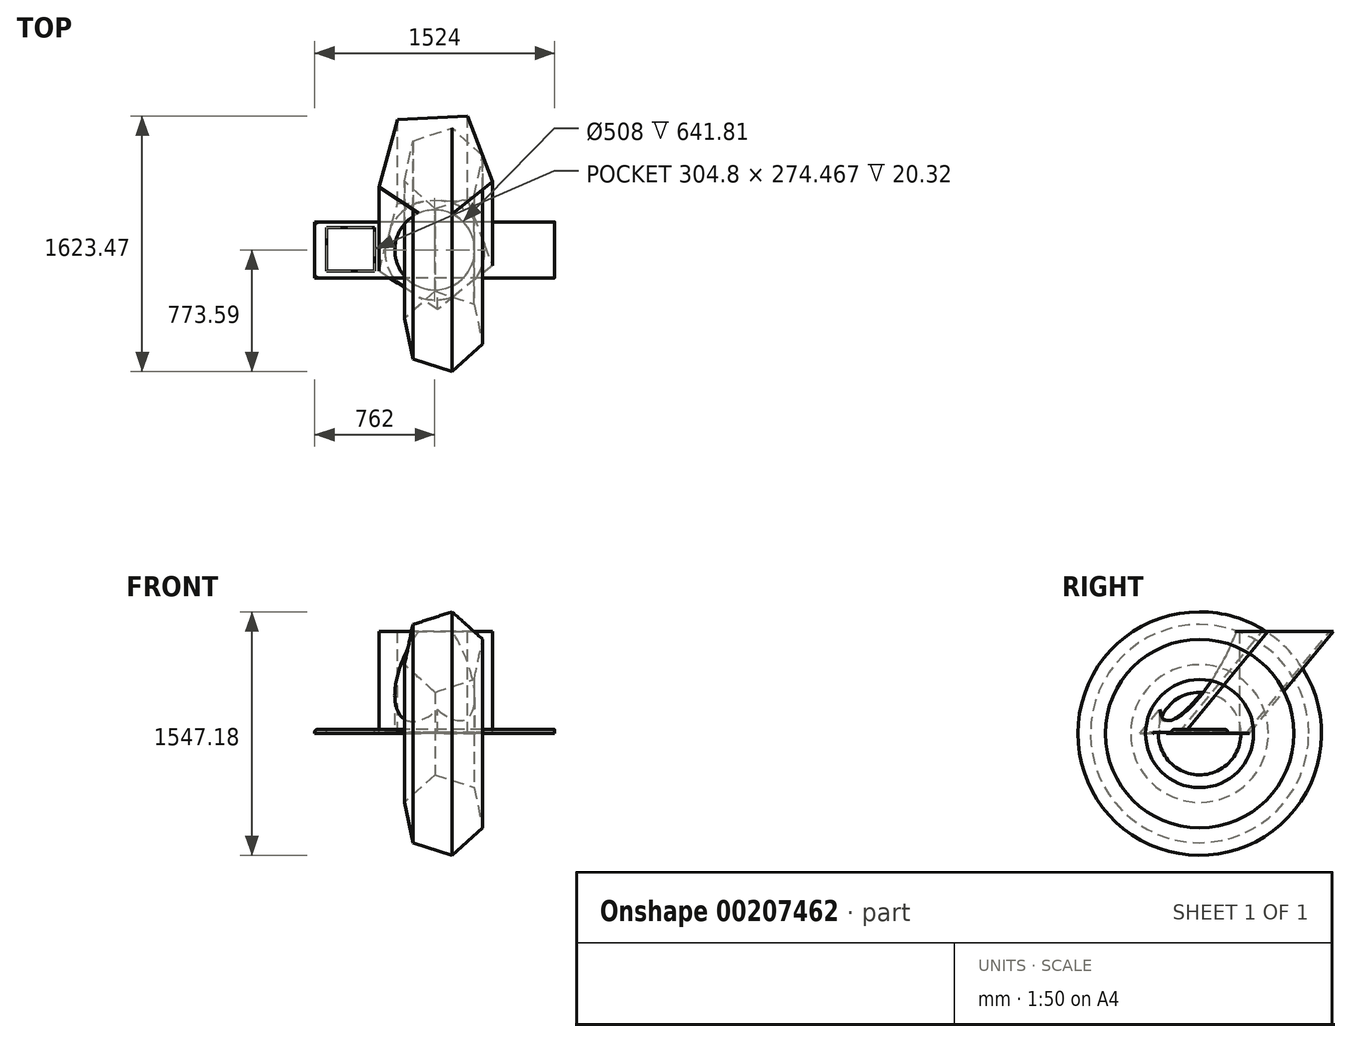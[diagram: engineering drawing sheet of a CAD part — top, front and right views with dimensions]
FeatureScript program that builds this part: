
annotation { "Feature Type Name" : "Feature", "Feature Type Description" : "" }
export const myFeature = defineFeature(function(context is Context, id is Id, definition is map)
    precondition{}
    {
        {
            var Q0;
            Q0=qCreatedBy(makeId("Top.planeOp"),FACE);
            var sketch = newSketch(context, id + "F0", { "sketchPlane" : qUnion([Q0])});
            skLineSegment(sketch, "E0.bottom", {"start": v(762, 177.8) * mm, "end": v(-762, 177.8) * mm});
            skLineSegment(sketch, "E0.top", {"start": v(762, -177.8) * mm, "end": v(-762, -177.8) * mm});
            skLineSegment(sketch, "E0.left", {"start": v(762, 177.8) * mm, "end": v(762, -177.8) * mm});
            skLineSegment(sketch, "E0.right", {"start": v(-762, 177.8) * mm, "end": v(-762, -177.8) * mm});
            skPoint(sketch, "E0.middle", {"position": v(0, 0) * mm});
            skSolve(sketch);
        }
        {
            var Q0;
            Q0=makeQuery(id+"F0.imprint","IMPRINT",FACE,{"disambiguationData":[TD([[makeQuery(id+"F0.imprint","IMPRINT",EDGE,{"derivedFrom":sQuery(id+"F0.wireOp",EDGE,"E0.bottom")}),1.0]])]});
            extrude(context, id + "F1", {"entities" : qUnion([Q0]), "depth" : 25.4 * mm});
        }
        {
            var Q0;
            Q0=makeQuery(id+"F1.opExtrude","CAP_FACE",FACE,{"disambiguationData":[OSD([sQuery(id+"F0.wireOp",EDGE,"E0.bottom"),sQuery(id+"F0.wireOp",EDGE,"E0.top"),sQuery(id+"F0.wireOp",EDGE,"E0.left"),sQuery(id+"F0.wireOp",EDGE,"E0.right")])],"isStart":false});
            var sketch = newSketch(context, id + "F2", { "sketchPlane" : qUnion([Q0])});
            skLineSegment(sketch, "E1.bottom", {"start": v(-685.8, -132.6) * mm, "end": v(-381, -132.6) * mm});
            skLineSegment(sketch, "E1.top", {"start": v(-685.8, 141.86) * mm, "end": v(-381, 141.86) * mm});
            skLineSegment(sketch, "E1.left", {"start": v(-685.8, -132.6) * mm, "end": v(-685.8, 141.86) * mm});
            skLineSegment(sketch, "E1.right", {"start": v(-381, -132.6) * mm, "end": v(-381, 141.86) * mm});
            skSolve(sketch);
        }
        {
            var Q0;
            Q0=makeQuery(id+"F2.imprint","IMPRINT",FACE,{"disambiguationData":[TD([[makeQuery(id+"F2.imprint","IMPRINT",EDGE,{"derivedFrom":sQuery(id+"F2.wireOp",EDGE,"E1.bottom")}),1.0]])]});
            extrude(context, id + "F3", {"entities" : qUnion([Q0]), "operationType" : NewBodyOperationType.REMOVE, "oppositeDirection" : true, "depth" : 20.32 * mm});
        }
        {
            var Q0;
            Q0=makeQuery(id+"F1.opExtrude","CAP_EDGE",EDGE,{"disambiguationData":[OSD([sQuery(id+"F0.wireOp",EDGE,"E0.top")])],"isStart":false});
            var Q1;
            Q1=makeQuery(id+"F1.opExtrude","CAP_EDGE",EDGE,{"disambiguationData":[OSD([sQuery(id+"F0.wireOp",EDGE,"E0.right")])],"isStart":false});
            var Q2;
            Q2=makeQuery(id+"F1.opExtrude","CAP_EDGE",EDGE,{"disambiguationData":[OSD([sQuery(id+"F0.wireOp",EDGE,"E0.bottom")])],"isStart":false});
            fillet(context, id + "F4", {"entities" : qUnion([Q0, Q1, Q2]), "radius" : 12.7 * mm, "tangentPropagation" : true, "allowEdgeOverflow" : false});
        }
        {
            var Q0;
            Q0=qCreatedBy(makeId("Top.planeOp"),FACE);
            var sketch = newSketch(context, id + "F5", { "sketchPlane" : qUnion([Q0])});
            skLineSegment(sketch, "E2", {"start": v(0, 0) * mm, "end": v(1065.77, 0) * mm, "construction": true});
            skCircle(sketch, "E3.cCircle", {"center": v(55.36, 518.03) * mm, "radius": 226.28 * mm, "construction": true});
            skLineSegment(sketch, "E3.0", {"start": v(303.87, 598.72) * mm, "end": v(249.5, 343.16) * mm});
            skLineSegment(sketch, "E3.1", {"start": v(249.5, 343.16) * mm, "end": v(0.98, 262.47) * mm});
            skLineSegment(sketch, "E3.2", {"start": v(0.98, 262.47) * mm, "end": v(-193.15, 437.34) * mm});
            skLineSegment(sketch, "E3.3", {"start": v(-193.15, 437.34) * mm, "end": v(-138.77, 692.9) * mm});
            skLineSegment(sketch, "E3.4", {"start": v(-138.77, 692.9) * mm, "end": v(109.74, 773.6) * mm});
            skLineSegment(sketch, "E3.5", {"start": v(109.74, 773.6) * mm, "end": v(303.87, 598.72) * mm});
            skPoint(sketch, "E3.0.midPoint", {"position": v(276.68, 470.94) * mm});
            skSolve(sketch);
        }
        {
            var Q0;
            Q0 = qSketchRegion(id + "F5", true);
            var Q1;
            Q1=sQuery(id+"F5.wireOp",EDGE,"E2");
            revolve(context, id + "F6", {"entities" : qUnion([Q0]), "axis" : qUnion([Q1]), "revolveType" : RevolveType.FULL});
        }
        {
            var Q0;
            Q0=qCreatedBy(makeId("Top.planeOp"),FACE);
            var sketch = newSketch(context, id + "F7", { "sketchPlane" : qUnion([Q0])});
            skCircle(sketch, "E4.cCircle", {"center": v(0, 0) * mm, "radius": 306.7 * mm, "construction": true});
            skLineSegment(sketch, "E4.0", {"start": v(365.82, -99.48) * mm, "end": v(18.43, -378.66) * mm});
            skLineSegment(sketch, "E4.1", {"start": v(18.43, -378.66) * mm, "end": v(-354.43, -134.54) * mm});
            skLineSegment(sketch, "E4.2", {"start": v(-354.43, -134.54) * mm, "end": v(-237.48, 295.5) * mm});
            skLineSegment(sketch, "E4.3", {"start": v(-237.48, 295.5) * mm, "end": v(207.66, 317.18) * mm});
            skLineSegment(sketch, "E4.4", {"start": v(207.66, 317.18) * mm, "end": v(365.82, -99.48) * mm});
            skPoint(sketch, "E4.0.midPoint", {"position": v(192.13, -239.07) * mm});
            skSolve(sketch);
        }
        {
            var Q0;
            Q0=qCreatedBy(makeId("Right.planeOp"),FACE);
            var sketch = newSketch(context, id + "F8", { "sketchPlane" : qUnion([Q0])});
            skLineSegment(sketch, "E5", {"start": v(0, 0) * mm, "end": v(532.7, 648.16) * mm});
            skLineSegment(sketch, "E6", {"start": v(572.6, 647.34) * mm, "end": v(991.86, 92.32) * mm});
            skLineSegment(sketch, "E7", {"start": v(1034.6, 95.8) * mm, "end": v(1183.12, 378.02) * mm});
            skPoint(sketch, "E8.visualSharp", {"position": v(553.17, 673.06) * mm});
            skArc(sketch, "E8.filletArc", {"start": v(572.6, 647.34) * mm, "mid": v(552.85, 657.43) * mm, "end": v(532.7, 648.16) * mm});
            skPoint(sketch, "E9.visualSharp", {"position": v(1015.97, 60.4) * mm});
            skArc(sketch, "E9.filletArc", {"start": v(991.86, 92.32) * mm, "mid": v(1014.19, 82.32) * mm, "end": v(1034.6, 95.8) * mm});
            skSolve(sketch);
        }
        {
            var Q0;
            Q0=makeQuery(id+"F7.imprint","IMPRINT",FACE,{"disambiguationData":[TD([[makeQuery(id+"F7.imprint","IMPRINT",EDGE,{"derivedFrom":sQuery(id+"F7.wireOp",EDGE,"E4.0")}),-1.0]])]});
            var Q1;
            Q1=sQuery(id+"F8.wireOp",EDGE,"E5");
            sweep(context, id + "F9", {"profiles" : qUnion([Q0]), "path" : qUnion([Q1])});
        }
        {
            var Q0;
            Q0=sQuery(id+"F7.wireOp",VERTEX,"E4.cCircle.center");
            var Q1;
            Q1=makeQuery(id+"F9.opSweep","SWEPT_BODY",BODY,{"disambiguationData":[OSD([sQuery(id+"F7.wireOp",EDGE,"E4.0"),sQuery(id+"F7.wireOp",EDGE,"E4.1"),sQuery(id+"F7.wireOp",EDGE,"E4.2"),sQuery(id+"F7.wireOp",EDGE,"E4.3"),sQuery(id+"F7.wireOp",EDGE,"E4.4"),sQuery(id+"F8.wireOp",EDGE,"E5")])]});
            hole(context, id + "F10", {"style" : HoleStyle.C_BORE, "endStyle" : HoleEndStyle.THROUGH, "oppositeDirection" : true, "holeDiameter" : 508 * mm, "cBoreDiameter" : 635 * mm, "cBoreDepth" : 6.35 * mm, "locations" : qUnion([Q0]), "scope" : qUnion([Q1]), "isTappedThrough" : true});
        }
    });
